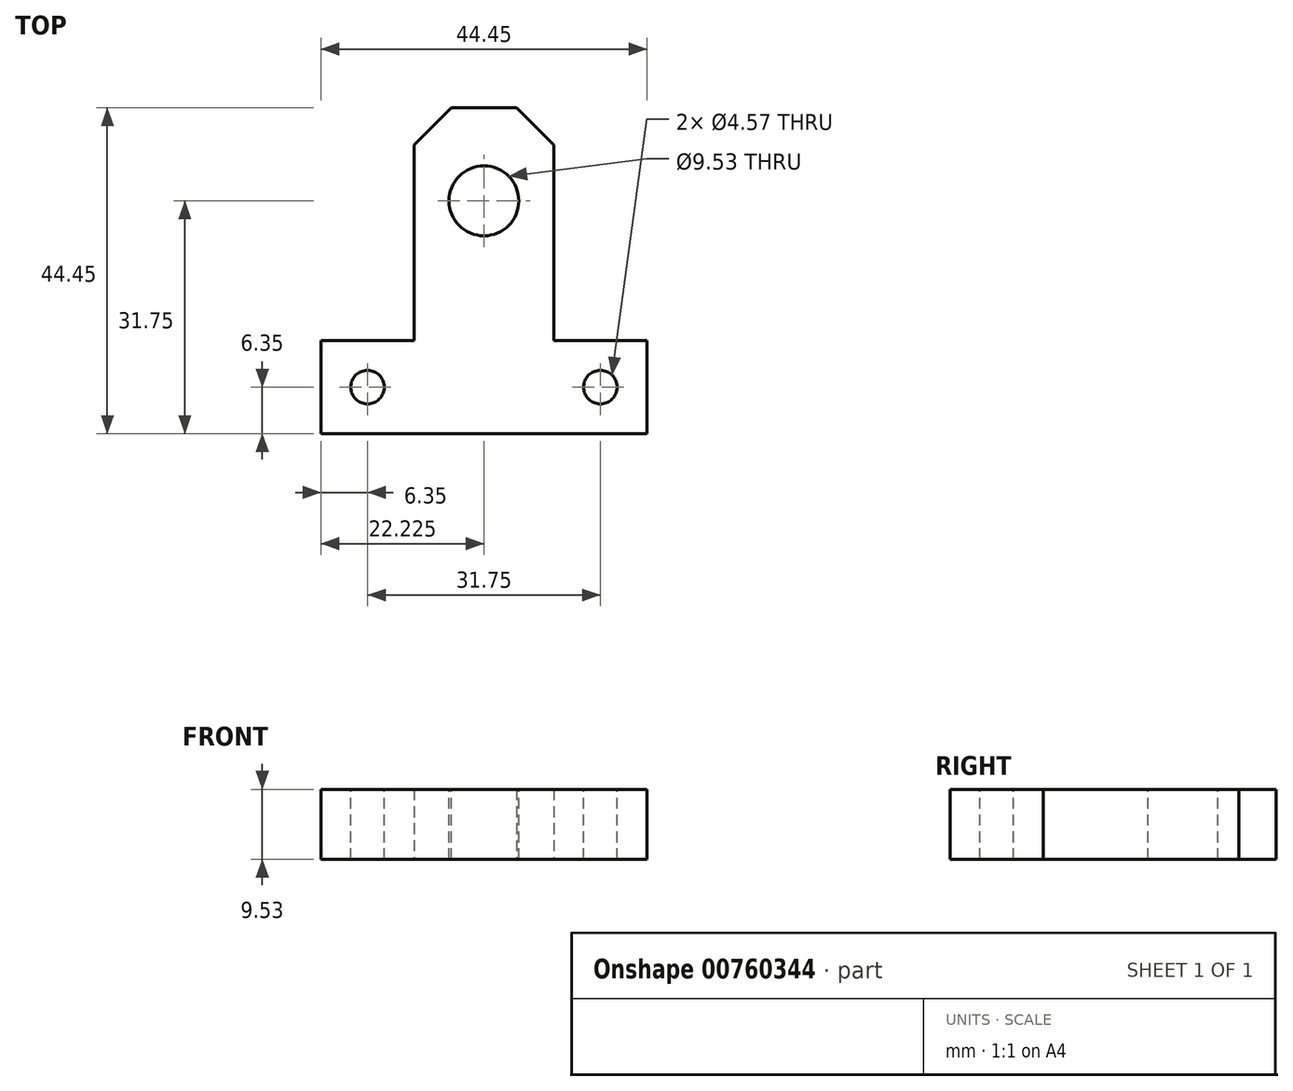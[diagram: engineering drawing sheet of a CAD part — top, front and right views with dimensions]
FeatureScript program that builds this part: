
annotation { "Feature Type Name" : "Feature", "Feature Type Description" : "" }
export const myFeature = defineFeature(function(context is Context, id is Id, definition is map)
    precondition{}
    {
        {
            var Q0;
            Q0=qCreatedBy(makeId("Top.planeOp"),FACE);
            var sketch = newSketch(context, id + "F0", { "sketchPlane" : qUnion([Q0])});
            skLineSegment(sketch, "E0", {"start": v(0, 0) * mm, "end": v(44.45, 0) * mm});
            skLineSegment(sketch, "E1", {"start": v(44.45, 0) * mm, "end": v(44.45, 12.7) * mm});
            skLineSegment(sketch, "E2", {"start": v(44.45, 12.7) * mm, "end": v(31.75, 12.7) * mm});
            skLineSegment(sketch, "E3", {"start": v(31.75, 12.7) * mm, "end": v(31.75, 44.45) * mm});
            skLineSegment(sketch, "E4", {"start": v(31.75, 44.45) * mm, "end": v(12.7, 44.45) * mm});
            skLineSegment(sketch, "E5", {"start": v(12.7, 44.45) * mm, "end": v(12.7, 12.7) * mm});
            skLineSegment(sketch, "E6", {"start": v(12.7, 12.7) * mm, "end": v(0, 12.7) * mm});
            skLineSegment(sketch, "E7", {"start": v(0, 12.7) * mm, "end": v(0, 0) * mm});
            skSolve(sketch);
        }
        {
            var Q0;
            Q0=makeQuery(id+"F0.imprint","IMPRINT",FACE,{"disambiguationData":[TD([[makeQuery(id+"F0.imprint","IMPRINT",EDGE,{"derivedFrom":sQuery(id+"F0.wireOp",EDGE,"E0")}),1.0]])]});
            extrude(context, id + "F1", {"entities" : qUnion([Q0]), "depth" : 9.52 * mm, "offsetDistance" : 25.4 * mm});
        }
        {
            var Q0;
            Q0=makeQuery(id+"F1.opExtrude","CAP_FACE",FACE,{"disambiguationData":[OSD([sQuery(id+"F0.wireOp",EDGE,"E0"),sQuery(id+"F0.wireOp",EDGE,"E1"),sQuery(id+"F0.wireOp",EDGE,"E2"),sQuery(id+"F0.wireOp",EDGE,"E3"),sQuery(id+"F0.wireOp",EDGE,"E4"),sQuery(id+"F0.wireOp",EDGE,"E5"),sQuery(id+"F0.wireOp",EDGE,"E6"),sQuery(id+"F0.wireOp",EDGE,"E7")])],"isStart":false});
            var sketch = newSketch(context, id + "F2", { "sketchPlane" : qUnion([Q0])});
            skLineSegment(sketch, "E8", {"start": v(22.23, 44.45) * mm, "end": v(22.23, 0) * mm, "construction": true});
            skLineSegment(sketch, "E9", {"start": v(0, 6.35) * mm, "end": v(44.45, 6.35) * mm, "construction": true});
            skCircle(sketch, "E10", {"center": v(22.23, 31.75) * mm, "radius": 4.76 * mm});
            skCircle(sketch, "E11", {"center": v(6.35, 6.35) * mm, "radius": 2.29 * mm});
            skCircle(sketch, "E12", {"center": v(38.1, 6.35) * mm, "radius": 2.29 * mm});
            skSolve(sketch);
        }
        {
            var Q0;
            Q0 = qSketchRegion(id + "F2", true);
            extrude(context, id + "F3", {"entities" : qUnion([Q0]), "operationType" : NewBodyOperationType.REMOVE, "oppositeDirection" : true, "depth" : 25.4 * mm, "offsetDistance" : 25.4 * mm});
        }
        {
            var Q0;
            Q0=makeQuery(id+"F1.opExtrude","SWEPT_EDGE",EDGE,{"disambiguationData":[OSD([sQuery(id+"F0.wireOp",EDGE,"E4"),sQuery(id+"F0.wireOp",EDGE,"E5")])]});
            var Q1;
            Q1=makeQuery(id+"F1.opExtrude","SWEPT_EDGE",EDGE,{"disambiguationData":[OSD([sQuery(id+"F0.wireOp",EDGE,"E3"),sQuery(id+"F0.wireOp",EDGE,"E4")])]});
            chamfer(context, id + "F4", {"entities" : qUnion([Q0, Q1]), "width" : 5.08 * mm, "tangentPropagation" : true});
        }
    });
